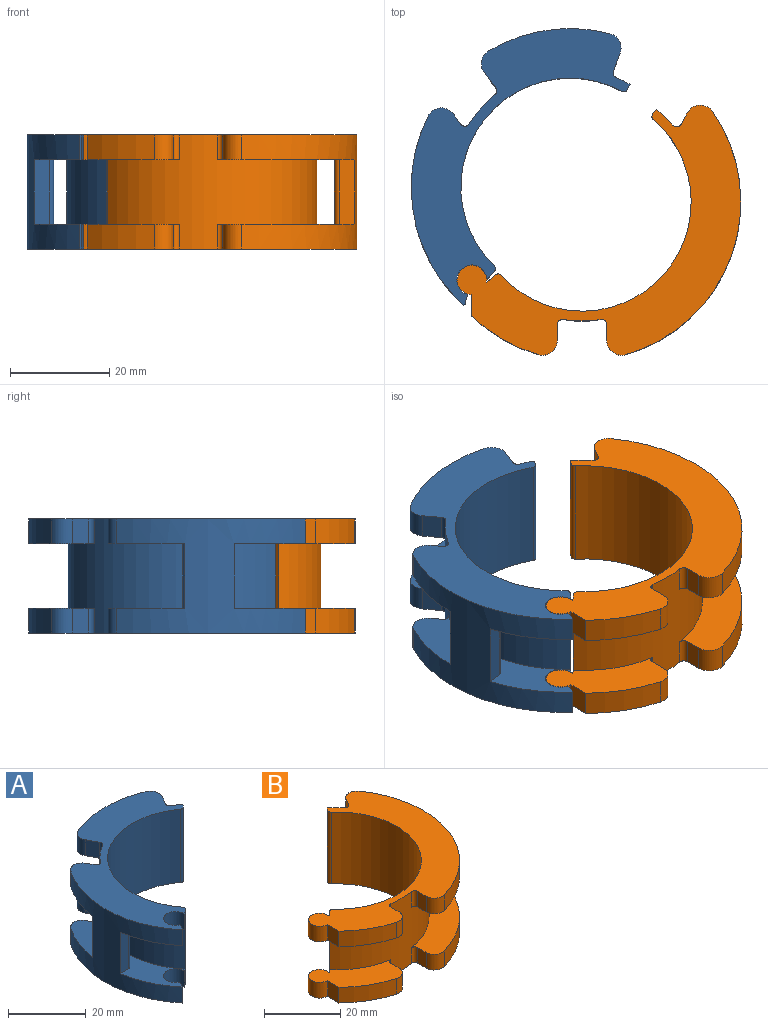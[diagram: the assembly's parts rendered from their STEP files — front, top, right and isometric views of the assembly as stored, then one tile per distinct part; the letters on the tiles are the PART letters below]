
ASSEMBLY  parts=2 mates=1
PART A: 44 faces, bbox 46.9x52.5x23 mm
  f0: cylinder r=3.05mm len=6.1mm, axis (0,0,1), area 67mm2, adj f2,f5,f18,f27
  f1: cylinder r=3.05mm len=6.1mm, axis (0,0,1), area 67mm2, adj f3,f4,f18,f26
  f2: plane 40.06x13.29mm, normal (0,0,-1), area 238.8mm2, adj f0,f6,f7,f8,f9,f12,f17,f18
  f3: plane 40.06x13.29mm, normal (0,0,1), area 238.8mm2, adj f1,f6,f7,f8,f12,f13,f18,f19
  f4: plane 52.53x46.94mm, normal (0,0,-1), area 636.7mm2, adj f1,f11,f12,f13,f18,f19,f20,f22
  f5: plane 52.53x46.94mm, normal (0,0,1), area 636.7mm2, adj f0,f9,f10,f12,f14,f16,f17,f18
  f6: plane 13x3.11mm, normal (0,-1,0), area 40.4mm2, adj f2,f3,f12,f31
  f7: plane 13x8mm, normal (1,0,0), area 104mm2, adj f2,f3,f30,f31
  f8: plane 13x3.11mm, normal (0,1,0), area 40.4mm2, adj f2,f3,f12,f30
  f9: plane 5x0.28mm, normal (0.64,-0.77,0), area 1.8mm2, adj f2,f5,f12,f27
  f10: cylinder r=32mm len=24.69mm, axis (0,0,-1), area 126.7mm2, adj f5,f15,f38,f40
  f11: cylinder r=32mm len=24.69mm, axis (0,0,-1), area 126.7mm2, adj f4,f21,f41,f43
  f12: cylinder r=32mm len=38.76mm, axis (0,0,-1), area 547.4mm2, adj f2,f3,f4,f5,f6,f8,f9,f13
  f13: plane 5x0.28mm, normal (0.64,-0.77,0), area 1.8mm2, adj f3,f4,f12,f26
  f14: plane 5x3.39mm, normal (0.88,-0.48,0), area 19.3mm2, adj f5,f15,f34,f40
  f15: plane 28.38x11.41mm, normal (0,0,-1), area 219.8mm2, adj f10,f14,f16,f24,f32,f34,f38,f40
  f16: plane 5x3.39mm, normal (-0.88,-0.48,0), area 19.3mm2, adj f5,f15,f32,f38
  f17: plane 5x2.28mm, normal (0.88,0.48,0), area 13mm2, adj f2,f5,f33,f39
  f18: plane 23x1.68mm, normal (0.64,-0.77,0), area 37.8mm2, adj f0,f1,f2,f3,f4,f5,f24,f29
  f19: plane 5x2.28mm, normal (0.88,0.48,0), area 13mm2, adj f3,f4,f36,f42
  f20: plane 5x3.39mm, normal (-0.88,-0.48,0), area 19.3mm2, adj f4,f21,f37,f43
  f21: plane 28.38x11.41mm, normal (0,0,1), area 219.8mm2, adj f11,f20,f22,f24,f35,f37,f41,f43
  f22: plane 5x3.39mm, normal (0.88,-0.48,0), area 19.3mm2, adj f4,f21,f35,f41
  f23: cylinder r=22mm len=35.5mm, axis (0,0,-1), area 1451.5mm2, adj f4,f5,f28,f29
  f24: cylinder r=24mm len=39.39mm, axis (0,0,1), area 1027.5mm2, adj f2,f3,f4,f5,f15,f18,f21,f25
  f25: plane 23x0.95mm, normal (0.78,-0.62,0), area 28mm2, adj f4,f5,f24,f28
  f26: plane 5x1.8mm, normal (0.91,-0.41,0), area 9.9mm2, adj f1,f3,f4,f13
  f27: plane 5x1.8mm, normal (0.91,-0.41,0), area 9.9mm2, adj f0,f2,f5,f9
  f28: cylinder r=0.8mm len=23mm, axis (0,0,-1), area 28.2mm2, adj f4,f5,f23,f25
  f29: cylinder r=0.8mm len=23mm, axis (0,0,-1), area 28.2mm2, adj f4,f5,f18,f23
  f30: cylinder r=1mm len=13mm, axis (0,0,1), area 20.4mm2, adj f2,f3,f7,f8
  f31: cylinder r=1mm len=13mm, axis (0,0,1), area 20.4mm2, adj f2,f3,f6,f7
  f32: cylinder r=1mm len=5mm, axis (0,0,1), area 7.7mm2, adj f5,f15,f16,f24
  f33: cylinder r=1mm len=5mm, axis (0,0,1), area 9.7mm2, adj f2,f5,f17,f24
  f34: cylinder r=1mm len=5mm, axis (0,0,1), area 7.7mm2, adj f5,f14,f15,f24
  f35: cylinder r=1mm len=5mm, axis (0,0,1), area 7.7mm2, adj f4,f21,f22,f24
  f36: cylinder r=1mm len=5mm, axis (0,0,1), area 9.7mm2, adj f3,f4,f19,f24
  f37: cylinder r=1mm len=5mm, axis (0,0,1), area 7.7mm2, adj f4,f20,f21,f24
  f38: cylinder r=3mm len=5mm, axis (0,0,-1), area 25.1mm2, adj f5,f10,f15,f16
  f39: cylinder r=3mm len=5.1mm, axis (0,0,-1), area 30.5mm2, adj f2,f5,f12,f17
  f40: cylinder r=3mm len=5mm, axis (0,0,-1), area 25.1mm2, adj f5,f10,f14,f15
  f41: cylinder r=3mm len=5mm, axis (0,0,-1), area 25.1mm2, adj f4,f11,f21,f22
  f42: cylinder r=3mm len=5.1mm, axis (0,0,-1), area 30.5mm2, adj f3,f4,f12,f19
  f43: cylinder r=3mm len=5mm, axis (0,0,-1), area 25.1mm2, adj f4,f11,f20,f21
PART B: 46 faces, bbox 57.2x50.4x23 mm
  f0: cylinder r=32mm len=13.48mm, axis (0,0,-1), area 78.7mm2, adj f3,f5,f28,f44
  f1: cylinder r=32mm len=13.48mm, axis (0,0,-1), area 78.7mm2, adj f2,f4,f29,f41
  f2: plane 57.15x50.4mm, normal (0,0,1), area 788.4mm2, adj f1,f7,f8,f9,f12,f16,f17,f18
  f3: plane 57.15x50.4mm, normal (0,0,-1), area 788.4mm2, adj f0,f6,f8,f9,f12,f13,f14,f15
  f4: plane 21.31x18.11mm, normal (0,0,-1), area 172.8mm2, adj f1,f7,f9,f16,f23,f25,f26,f29
  f5: plane 21.31x18.11mm, normal (0,0,1), area 172.8mm2, adj f0,f6,f9,f14,f22,f24,f26,f28
  f6: cylinder r=0.05mm len=5mm, axis (0,0,1), area 0.4mm2, adj f3,f5,f22,f28
  f7: cylinder r=0.05mm len=5mm, axis (0,0,1), area 0.4mm2, adj f2,f4,f23,f29
  f8: cylinder r=22mm len=38.66mm, axis (0,0,-1), area 1652.3mm2, adj f2,f3,f30,f31
  f9: cylinder r=24mm len=42.72mm, axis (0,0,1), area 1163.9mm2, adj f2,f3,f4,f5,f10,f11,f26,f27
  f10: plane 50.4x27.77mm, normal (0,0,-1), area 419.1mm2, adj f9,f12,f17,f18,f19,f20,f21,f32
  f11: plane 50.4x27.77mm, normal (0,0,1), area 419.1mm2, adj f9,f12,f13,f15,f19,f20,f21,f32
  f12: cylinder r=32mm len=48.99mm, axis (0,0,-1), area 737.8mm2, adj f2,f3,f10,f11,f19,f21,f40,f42
  f13: plane 5x3.2mm, normal (-1,0,0), area 16mm2, adj f3,f11,f37,f43
  f14: plane 5x3.2mm, normal (1,0,0), area 16mm2, adj f3,f5,f38,f44
  f15: plane 5x2.28mm, normal (-0.88,0.48,0), area 13mm2, adj f3,f11,f39,f45
  f16: plane 5x3.2mm, normal (1,0,0), area 16mm2, adj f2,f4,f35,f41
  f17: plane 5x3.2mm, normal (-1,0,0), area 16mm2, adj f2,f10,f36,f42
  f18: plane 5x2.28mm, normal (-0.88,0.48,0), area 13mm2, adj f2,f10,f34,f40
  f19: plane 13x3.11mm, normal (0,1,0), area 40.4mm2, adj f10,f11,f12,f32
  f20: plane 13x8mm, normal (-1,0,0), area 104mm2, adj f10,f11,f32,f33
  f21: plane 13x3.11mm, normal (0,-1,0), area 40.4mm2, adj f10,f11,f12,f33
  f22: cylinder r=2.95mm len=5.9mm, axis (0,0,1), area 71.2mm2, adj f3,f5,f6,f24
  f23: cylinder r=2.95mm len=5.9mm, axis (0,0,1), area 71.2mm2, adj f2,f4,f7,f25
  f24: cylinder r=0.05mm len=5mm, axis (0,0,1), area 0.6mm2, adj f3,f5,f22,f26
  f25: cylinder r=0.05mm len=5mm, axis (0,0,1), area 0.6mm2, adj f2,f4,f23,f26
  f26: plane 23x1.78mm, normal (-0.64,0.77,0), area 39mm2, adj f2,f3,f4,f5,f9,f24,f25,f31
  f27: plane 23x0.95mm, normal (-0.78,0.62,0), area 28mm2, adj f2,f3,f9,f30
  f28: plane 5x4.23mm, normal (-1,0.01,0), area 21.1mm2, adj f0,f3,f5,f6
  f29: plane 5x4.23mm, normal (-1,0.01,0), area 21.1mm2, adj f1,f2,f4,f7
  f30: cylinder r=0.8mm len=23mm, axis (0,0,-1), area 28.2mm2, adj f2,f3,f8,f27
  f31: cylinder r=0.8mm len=23mm, axis (0,0,-1), area 28.2mm2, adj f2,f3,f8,f26
  f32: cylinder r=1mm len=13mm, axis (0,0,1), area 20.4mm2, adj f10,f11,f19,f20
  f33: cylinder r=1mm len=13mm, axis (0,0,1), area 20.4mm2, adj f10,f11,f20,f21
  f34: cylinder r=1mm len=5mm, axis (0,0,1), area 9.7mm2, adj f2,f9,f10,f18
  f35: cylinder r=1mm len=5mm, axis (0,0,1), area 8.7mm2, adj f2,f4,f9,f16
  f36: cylinder r=1mm len=5mm, axis (0,0,1), area 8.7mm2, adj f2,f9,f10,f17
  f37: cylinder r=1mm len=5mm, axis (0,0,1), area 8.7mm2, adj f3,f9,f11,f13
  f38: cylinder r=1mm len=5mm, axis (0,0,1), area 8.7mm2, adj f3,f5,f9,f14
  f39: cylinder r=1mm len=5mm, axis (0,0,1), area 9.7mm2, adj f3,f9,f11,f15
  f40: cylinder r=3mm len=5.1mm, axis (0,0,-1), area 30.5mm2, adj f2,f10,f12,f18
  f41: cylinder r=3mm len=5mm, axis (0,0,-1), area 27.8mm2, adj f1,f2,f4,f16
  f42: cylinder r=3mm len=5mm, axis (0,0,-1), area 27.8mm2, adj f2,f10,f12,f17
  f43: cylinder r=3mm len=5mm, axis (0,0,-1), area 27.8mm2, adj f3,f11,f12,f13
  f44: cylinder r=3mm len=5mm, axis (0,0,-1), area 27.8mm2, adj f0,f3,f5,f14
  f45: cylinder r=3mm len=5.1mm, axis (0,0,-1), area 30.5mm2, adj f3,f11,f12,f15
PLACE A rot(axis=(0,0,1),8.1deg) t=(-2.44,2.98,0)mm
PLACE B at identity
MATE cylindrical A.f0 <-> B.f22  axis (0,0,1) through (-22.2,-15.71,18)mm
